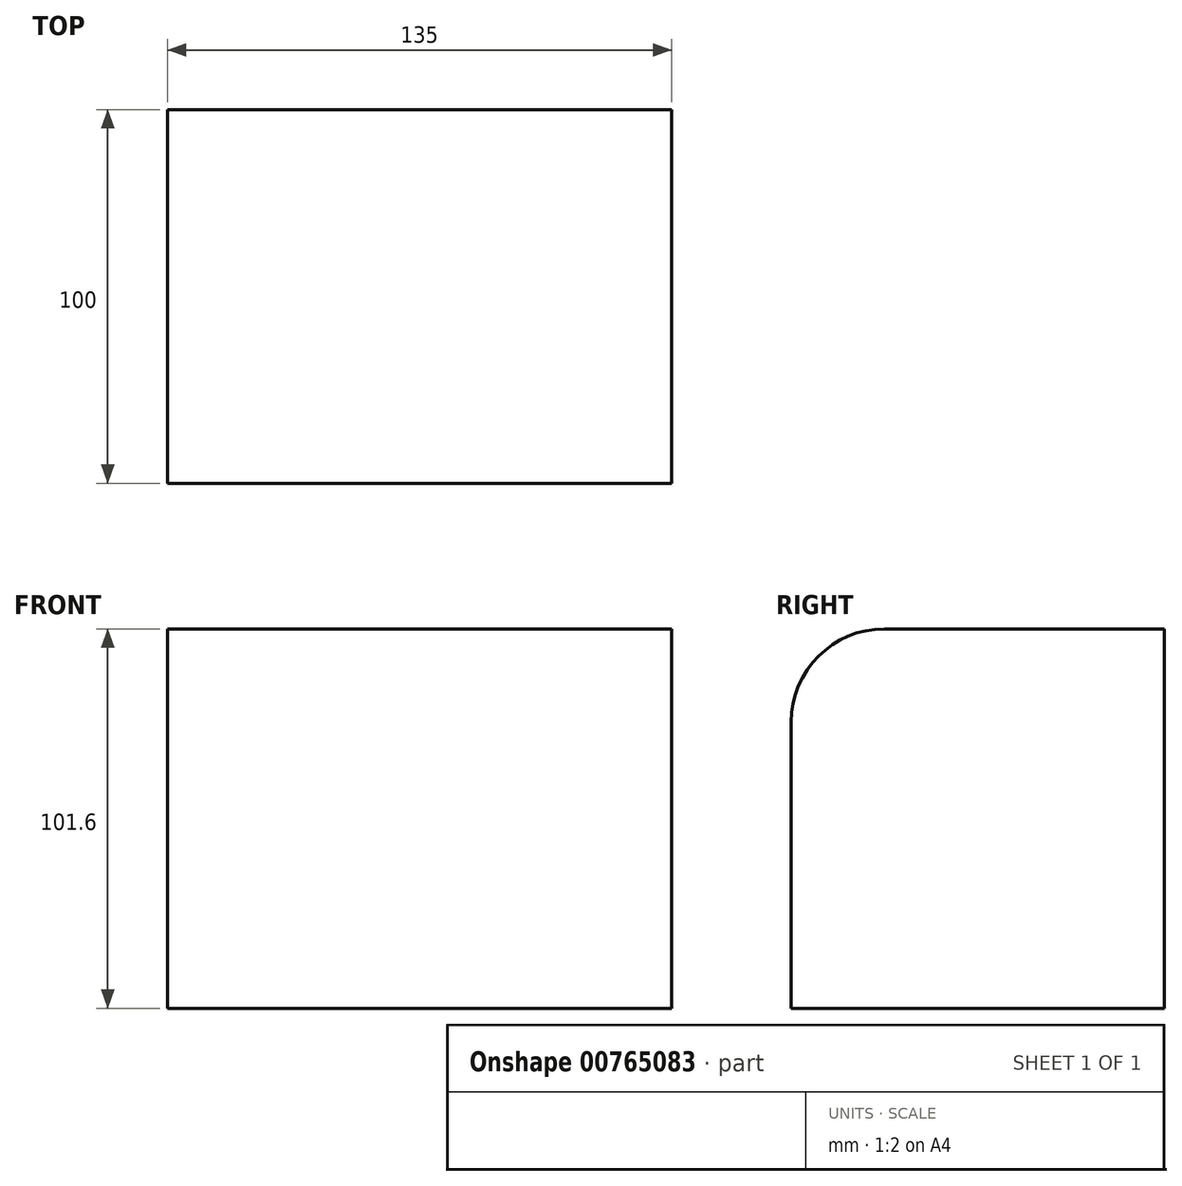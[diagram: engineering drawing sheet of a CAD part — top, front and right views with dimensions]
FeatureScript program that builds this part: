
annotation { "Feature Type Name" : "Feature", "Feature Type Description" : "" }
export const myFeature = defineFeature(function(context is Context, id is Id, definition is map)
    precondition{}
    {
        {
            var Q0;
            Q0=qCreatedBy(makeId("Front.planeOp"),FACE);
            var sketch = newSketch(context, id + "F0", { "sketchPlane" : qUnion([Q0])});
            skLineSegment(sketch, "E0.bottom", {"start": v(-135, 101.6) * mm, "end": v(0, 101.6) * mm});
            skLineSegment(sketch, "E0.top", {"start": v(-135, 0) * mm, "end": v(0, 0) * mm});
            skLineSegment(sketch, "E0.left", {"start": v(-135, 101.6) * mm, "end": v(-135, 0) * mm});
            skLineSegment(sketch, "E0.right", {"start": v(0, 101.6) * mm, "end": v(0, 0) * mm});
            skSolve(sketch);
        }
        {
            var Q0;
            Q0 = qSketchRegion(id + "F0", true);
            extrude(context, id + "F1", {"entities" : qUnion([Q0]), "depth" : 100 * mm, "offsetDistance" : 25 * mm});
        }
        {
            var Q0;
            Q0=makeQuery(id+"F1.opExtrude","CAP_EDGE",EDGE,{"disambiguationData":[OSD([sQuery(id+"F0.wireOp",EDGE,"E0.bottom")])],"isStart":false});
            fillet(context, id + "F2", {"entities" : qUnion([Q0]), "radius" : 25 * mm, "tangentPropagation" : true, "allowEdgeOverflow" : false});
        }
    });
